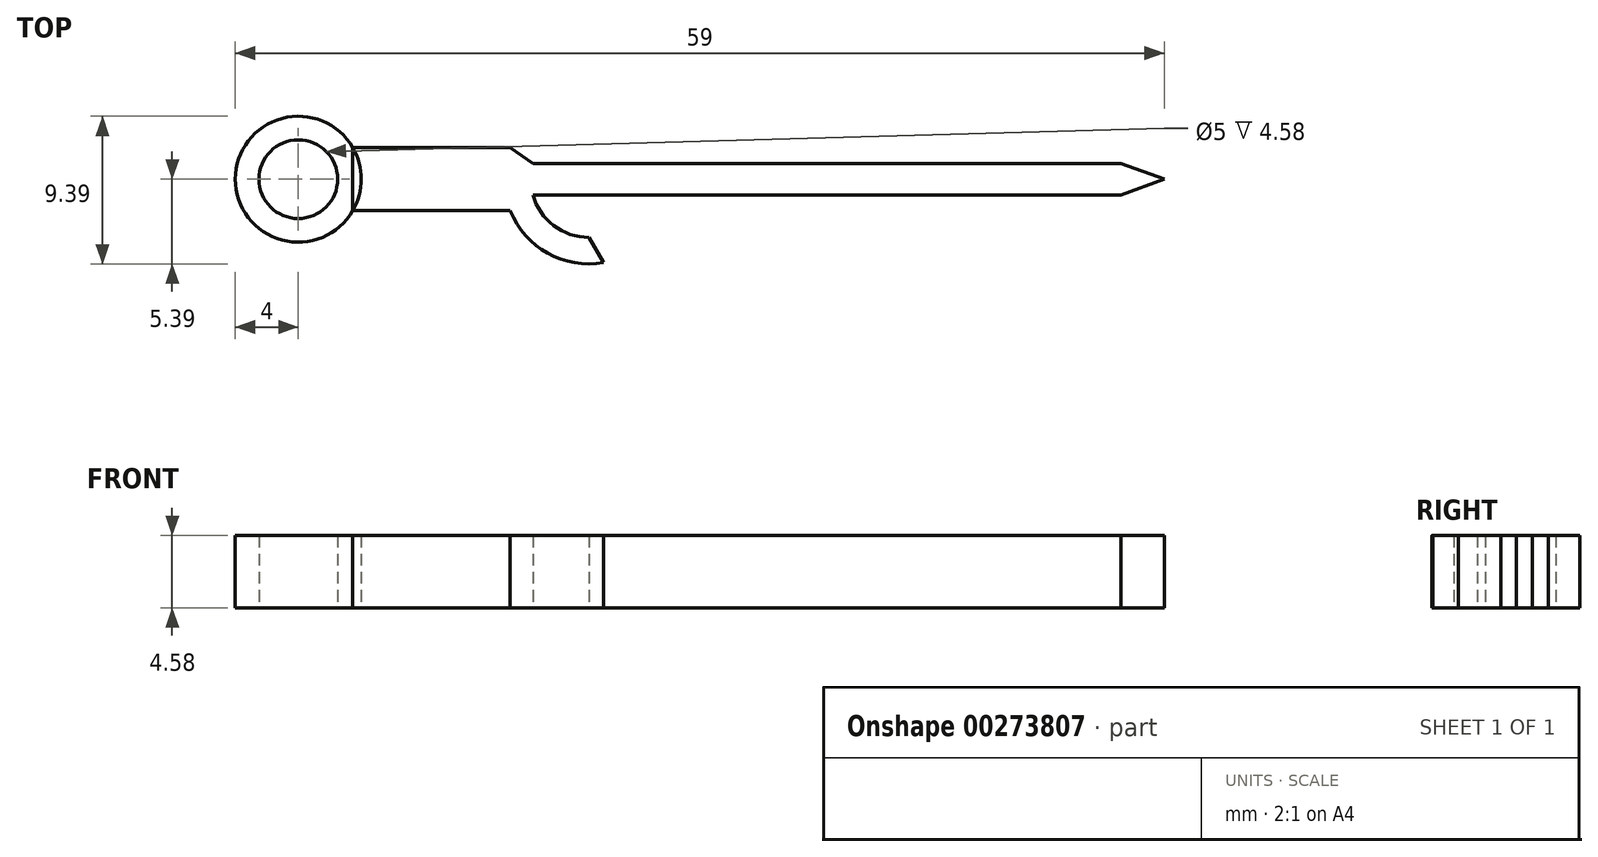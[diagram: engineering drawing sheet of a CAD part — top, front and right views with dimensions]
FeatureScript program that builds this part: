
annotation { "Feature Type Name" : "Feature", "Feature Type Description" : "" }
export const myFeature = defineFeature(function(context is Context, id is Id, definition is map)
    precondition{}
    {
        {
            var Q0;
            Q0=qCreatedBy(makeId("Top.planeOp"),FACE);
            var sketch = newSketch(context, id + "F0", { "sketchPlane" : qUnion([Q0])});
            skLineSegment(sketch, "E0", {"start": v(0, 0) * mm, "end": v(55, 0) * mm});
            skCircle(sketch, "E1", {"center": v(0, 0) * mm, "radius": 4 * mm});
            skCircle(sketch, "E2", {"center": v(0, 0) * mm, "radius": 2.5 * mm});
            skPoint(sketch, "E3", {"position": v(3.46, 0) * mm});
            skLineSegment(sketch, "E4", {"start": v(3.46, 2) * mm, "end": v(3.46, -2) * mm});
            skPoint(sketch, "E5", {"position": v(13.46, 0) * mm});
            skLineSegment(sketch, "E6", {"start": v(3.46, 0) * mm, "end": v(13.46, 0) * mm});
            skLineSegment(sketch, "E7", {"start": v(13.46, 2) * mm, "end": v(13.46, -2) * mm});
            skLineSegment(sketch, "E8", {"start": v(3.46, 2) * mm, "end": v(13.46, 2) * mm});
            skLineSegment(sketch, "E9", {"start": v(3.46, -2) * mm, "end": v(13.46, -2) * mm});
            skPoint(sketch, "E10", {"position": v(16.34, 0) * mm});
            skLineSegment(sketch, "E11", {"start": v(13.46, 2) * mm, "end": v(16.34, 0) * mm});
            skLineSegment(sketch, "E12", {"start": v(16.34, 0) * mm, "end": v(13.46, -2) * mm});
            skPoint(sketch, "E13", {"position": v(14.42, 0) * mm});
            skLineSegment(sketch, "E14", {"start": v(14.9, 1) * mm, "end": v(13.46, -2) * mm});
            skLineSegment(sketch, "E15", {"start": v(13.46, 2) * mm, "end": v(14.9, -1) * mm});
            skPoint(sketch, "E16", {"position": v(18.46, 0) * mm});
            skArc(sketch, "E17", {"start": v(13.46, 2) * mm, "mid": v(15.84, 4.7) * mm, "end": v(19.39, 5.3) * mm});
            skArc(sketch, "E18", {"start": v(13.46, -2) * mm, "mid": v(15.84, -4.7) * mm, "end": v(19.39, -5.3) * mm});
            skLineSegment(sketch, "E19", {"start": v(19.39, -5.3) * mm, "end": v(18.46, -3.7) * mm});
            skLineSegment(sketch, "E20", {"start": v(19.39, 5.3) * mm, "end": v(18.46, 3.7) * mm});
            skArc(sketch, "E21", {"start": v(14.9, 1) * mm, "mid": v(16.23, 2.95) * mm, "end": v(18.46, 3.7) * mm});
            skArc(sketch, "E22", {"start": v(14.9, -1) * mm, "mid": v(16.23, -2.95) * mm, "end": v(18.46, -3.7) * mm});
            skLineSegment(sketch, "E23", {"start": v(14.9, -1) * mm, "end": v(52.25, -1) * mm});
            skLineSegment(sketch, "E24", {"start": v(14.9, 1) * mm, "end": v(52.25, 1) * mm});
            skLineSegment(sketch, "E25", {"start": v(55, 0) * mm, "end": v(52.25, 1) * mm});
            skLineSegment(sketch, "E26", {"start": v(55, 0) * mm, "end": v(52.25, -1) * mm});
            skPoint(sketch, "E27.visualSharp", {"position": v(14.9, -1) * mm});
            skPoint(sketch, "E28.visualSharp", {"position": v(14.9, 1) * mm});
            skSolve(sketch);
        }
        {
            var Q0;
            Q0=makeQuery(id+"F0.imprint","IMPRINT",FACE,{"disambiguationData":[TD([[makeQuery(id+"F0.imprint","IMPRINT",EDGE,{"derivedFrom":sQuery(id+"F0.wireOp",EDGE,"E2")}),-1.0]])]});
            var Q1;
            {var subQ0=sQuery(id+"F0.wireOp",EDGE,"E4");var subQ3=sQuery(id+"F0.wireOp",EDGE,"E6");var subQ5=makeQuery(id+"F0.imprint","INTERSECT",VERTEX,{"derivedFrom":[subQ0,subQ3]});Q1=makeQuery(id+"F0.imprint","IMPRINT",FACE,{"disambiguationData":[TD([[makeQuery(id+"F0.imprint","IMPRINT",EDGE,{"disambiguationData":[TD([[subQ5,-1.0]])],"derivedFrom":subQ3}),-1.0]])]});}
            var Q2;
            {var subQ0=sQuery(id+"F0.wireOp",EDGE,"E4");var subQ3=sQuery(id+"F0.wireOp",EDGE,"E6");var subQ5=makeQuery(id+"F0.imprint","INTERSECT",VERTEX,{"derivedFrom":[subQ0,subQ3]});Q2=makeQuery(id+"F0.imprint","IMPRINT",FACE,{"disambiguationData":[TD([[makeQuery(id+"F0.imprint","IMPRINT",EDGE,{"disambiguationData":[TD([[subQ5,-1.0]])],"derivedFrom":subQ3}),1.0]])]});}
            var Q3;
            {var subQ0=sQuery(id+"F0.wireOp",EDGE,"E9");Q3=makeQuery(id+"F0.imprint","IMPRINT",FACE,{"disambiguationData":[TD([[makeQuery(id+"F0.imprint","IMPRINT",EDGE,{"derivedFrom":subQ0}),1.0]])]});}
            var Q4;
            {var subQ0=sQuery(id+"F0.wireOp",EDGE,"E8");Q4=makeQuery(id+"F0.imprint","IMPRINT",FACE,{"disambiguationData":[TD([[makeQuery(id+"F0.imprint","IMPRINT",EDGE,{"derivedFrom":subQ0}),-1.0]])]});}
            var Q5;
            {var subQ0=sQuery(id+"F0.wireOp",EDGE,"E7");var subQ1=sQuery(id+"F0.wireOp",EDGE,"E0");var subQ2=makeQuery(id+"F0.imprint","INTERSECT",VERTEX,{"derivedFrom":[subQ1,sQuery(id+"F0.wireOp",EDGE,"E6"),subQ0]});Q5=makeQuery(id+"F0.imprint","IMPRINT",FACE,{"disambiguationData":[TD([[makeQuery(id+"F0.imprint","IMPRINT",EDGE,{"disambiguationData":[TD([[subQ2,-1.0]])],"derivedFrom":subQ1}),-1.0]])]});}
            var Q6;
            {var subQ0=sQuery(id+"F0.wireOp",EDGE,"E7");var subQ1=sQuery(id+"F0.wireOp",EDGE,"E0");var subQ2=makeQuery(id+"F0.imprint","INTERSECT",VERTEX,{"derivedFrom":[subQ1,sQuery(id+"F0.wireOp",EDGE,"E6"),subQ0]});Q6=makeQuery(id+"F0.imprint","IMPRINT",FACE,{"disambiguationData":[TD([[makeQuery(id+"F0.imprint","IMPRINT",EDGE,{"disambiguationData":[TD([[subQ2,-1.0]])],"derivedFrom":subQ1}),1.0]])]});}
            var Q7;
            {var subQ0=sQuery(id+"F0.wireOp",EDGE,"E12");var subQ1=sQuery(id+"F0.wireOp",EDGE,"E0");var subQ2=makeQuery(id+"F0.imprint","INTERSECT",VERTEX,{"derivedFrom":[subQ1,sQuery(id+"F0.wireOp",EDGE,"E11"),subQ0]});Q7=makeQuery(id+"F0.imprint","IMPRINT",FACE,{"disambiguationData":[TD([[makeQuery(id+"F0.imprint","IMPRINT",EDGE,{"disambiguationData":[TD([[subQ2,1.0]])],"derivedFrom":subQ1}),-1.0]])]});}
            var Q8;
            {var subQ0=sQuery(id+"F0.wireOp",EDGE,"E11");var subQ1=sQuery(id+"F0.wireOp",EDGE,"E0");var subQ2=makeQuery(id+"F0.imprint","INTERSECT",VERTEX,{"derivedFrom":[subQ1,subQ0,sQuery(id+"F0.wireOp",EDGE,"E12")]});Q8=makeQuery(id+"F0.imprint","IMPRINT",FACE,{"disambiguationData":[TD([[makeQuery(id+"F0.imprint","IMPRINT",EDGE,{"disambiguationData":[TD([[subQ2,1.0]])],"derivedFrom":subQ1}),1.0]])]});}
            var Q9;
            {var subQ0=sQuery(id+"F0.wireOp",EDGE,"E14");var subQ3=sQuery(id+"F0.wireOp",EDGE,"E15");var subQ5=makeQuery(id+"F0.imprint","INTERSECT",VERTEX,{"derivedFrom":[sQuery(id+"F0.wireOp",EDGE,"E0"),subQ0,subQ3]});Q9=makeQuery(id+"F0.imprint","IMPRINT",FACE,{"disambiguationData":[TD([[makeQuery(id+"F0.imprint","IMPRINT",EDGE,{"disambiguationData":[TD([[subQ5,-1.0]])],"derivedFrom":subQ3}),-1.0]])]});}
            var Q10;
            {var subQ0=sQuery(id+"F0.wireOp",EDGE,"E18");Q10=makeQuery(id+"F0.imprint","IMPRINT",FACE,{"disambiguationData":[TD([[makeQuery(id+"F0.imprint","IMPRINT",EDGE,{"derivedFrom":subQ0}),1.0]])]});}
            var Q11;
            {var subQ4=sQuery(id+"F0.wireOp",EDGE,"E23");Q11=makeQuery(id+"F0.imprint","IMPRINT",FACE,{"disambiguationData":[TD([[makeQuery(id+"F0.imprint","IMPRINT",EDGE,{"derivedFrom":subQ4}),1.0]])]});}
            var Q12;
            {var subQ4=sQuery(id+"F0.wireOp",EDGE,"E24");Q12=makeQuery(id+"F0.imprint","IMPRINT",FACE,{"disambiguationData":[TD([[makeQuery(id+"F0.imprint","IMPRINT",EDGE,{"derivedFrom":subQ4}),-1.0]])]});}
            var Q13;
            {var subQ0=sQuery(id+"F0.wireOp",EDGE,"E17");Q13=makeQuery(id+"F0.imprint","IMPRINT",FACE,{"disambiguationData":[TD([[makeQuery(id+"F0.imprint","IMPRINT",EDGE,{"derivedFrom":subQ0}),-1.0]])]});}
            var Q14;
            {var subQ0=sQuery(id+"F0.wireOp",EDGE,"E15");var subQ3=sQuery(id+"F0.wireOp",EDGE,"E14");var subQ5=makeQuery(id+"F0.imprint","INTERSECT",VERTEX,{"derivedFrom":[sQuery(id+"F0.wireOp",EDGE,"E0"),subQ3,subQ0]});Q14=makeQuery(id+"F0.imprint","IMPRINT",FACE,{"disambiguationData":[TD([[makeQuery(id+"F0.imprint","IMPRINT",EDGE,{"disambiguationData":[TD([[subQ5,1.0]])],"derivedFrom":subQ3}),-1.0]])]});}
            extrude(context, id + "F1", {"entities" : qUnion([Q0, Q1, Q2, Q3, Q4, Q5, Q6, Q7, Q8, Q9, Q10, Q11, Q12, Q13, Q14]), "endBound" : BoundingType.SYMMETRIC, "depth" : 4.58 * mm});
        }
    });
